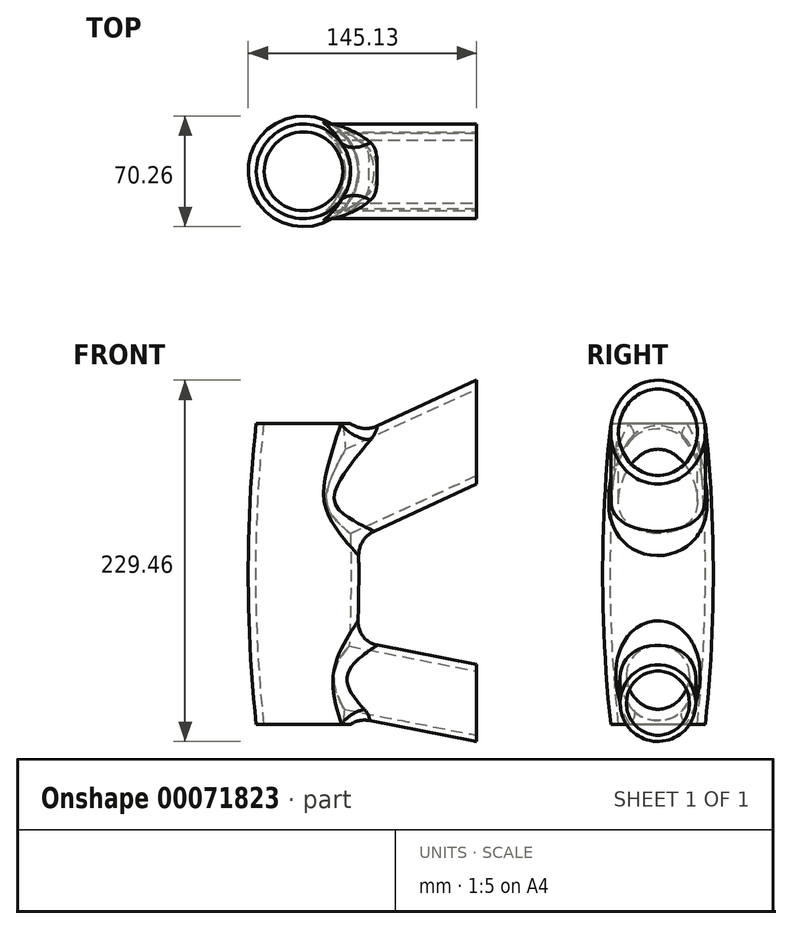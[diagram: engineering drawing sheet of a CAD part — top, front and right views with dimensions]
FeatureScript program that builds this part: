
annotation { "Feature Type Name" : "Feature", "Feature Type Description" : "" }
export const myFeature = defineFeature(function(context is Context, id is Id, definition is map)
    precondition{}
    {
        {
            var Q0;
            Q0=qCreatedBy(makeId("Front.planeOp"),FACE);
            var sketch = newSketch(context, id + "F0", { "sketchPlane" : qUnion([Q0])});
            skLineSegment(sketch, "E0", {"start": v(0, -80) * mm, "end": v(-30, -80) * mm, "construction": true});
            skLineSegment(sketch, "E1", {"start": v(0, 111) * mm, "end": v(-30, 111) * mm, "construction": true});
            skLineSegment(sketch, "E2", {"start": v(0, 111) * mm, "end": v(0, 0) * mm, "construction": true});
            skLineSegment(sketch, "E3", {"start": v(0, 0) * mm, "end": v(0, -80) * mm, "construction": true});
            skLineSegment(sketch, "E4", {"start": v(0, 0) * mm, "end": v(-35, 0) * mm, "construction": true});
            skArc(sketch, "E5", {"start": v(-30, 111) * mm, "mid": v(-35.13, 15.5) * mm, "end": v(-30, -80) * mm});
            skLineSegment(sketch, "E6", {"start": v(0, 0) * mm, "end": v(-25.5, 0) * mm, "construction": true});
            skLineSegment(sketch, "E7", {"start": v(0, 111) * mm, "end": v(-20.5, 111) * mm, "construction": true});
            skLineSegment(sketch, "E8", {"start": v(0, -80) * mm, "end": v(-20.5, -80) * mm, "construction": true});
            skLineSegment(sketch, "E9", {"start": v(-20.5, 111) * mm, "end": v(-30, 111) * mm});
            skLineSegment(sketch, "E10", {"start": v(-20.5, -80) * mm, "end": v(-30, -80) * mm});
            skLineSegment(sketch, "E11", {"start": v(-20.5, 111) * mm, "end": v(0, 111) * mm});
            skLineSegment(sketch, "E12", {"start": v(0, 111) * mm, "end": v(0, -80) * mm});
            skLineSegment(sketch, "E13", {"start": v(0, -80) * mm, "end": v(-20.5, -80) * mm});
            skSolve(sketch);
        }
        {
            var Q0;
            Q0=makeQuery(id+"F0.imprint","IMPRINT",FACE,{"disambiguationData":[TD([[makeQuery(id+"F0.imprint","IMPRINT",EDGE,{"derivedFrom":sQuery(id+"F0.wireOp",EDGE,"E5")}),1.0]])]});
            var Q1;
            Q1=sQuery(id+"F0.wireOp",EDGE,"E2");
            revolve(context, id + "F1", {"entities" : qUnion([Q0]), "axis" : qUnion([Q1]), "revolveType" : RevolveType.FULL});
        }
        {
            var Q0;
            Q0=qCreatedBy(makeId("Front.planeOp"),FACE);
            var sketch = newSketch(context, id + "F2", { "sketchPlane" : qUnion([Q0])});
            skLineSegment(sketch, "E14", {"start": v(0, 0) * mm, "end": v(0, 55) * mm, "construction": true});
            skLineSegment(sketch, "E15", {"start": v(0, 55) * mm, "end": v(154.46, 126) * mm, "construction": true});
            skLineSegment(sketch, "E16", {"start": v(0, 55) * mm, "end": v(0, 126) * mm, "construction": true});
            skLineSegment(sketch, "E17", {"start": v(0, 126) * mm, "end": v(154.46, 126) * mm, "construction": true});
            skLineSegment(sketch, "E18", {"start": v(154.46, 126) * mm, "end": v(167, 98.74) * mm, "construction": true});
            skLineSegment(sketch, "E19", {"start": v(0, 55) * mm, "end": v(12.53, 27.74) * mm, "construction": true});
            skLineSegment(sketch, "E20", {"start": v(154.46, 126) * mm, "end": v(164.07, 105.1) * mm, "construction": true});
            skLineSegment(sketch, "E21", {"start": v(0, 55) * mm, "end": v(9.6, 34.1) * mm, "construction": true});
            skLineSegment(sketch, "E22", {"start": v(12.53, 27.74) * mm, "end": v(167, 98.74) * mm});
            skLineSegment(sketch, "E23", {"start": v(9.6, 34.1) * mm, "end": v(12.53, 27.74) * mm});
            skLineSegment(sketch, "E24", {"start": v(164.07, 105.1) * mm, "end": v(167, 98.74) * mm});
            skLineSegment(sketch, "E25", {"start": v(9.6, 34.1) * mm, "end": v(0, 55) * mm});
            skLineSegment(sketch, "E26", {"start": v(0, 55) * mm, "end": v(154.46, 126) * mm});
            skLineSegment(sketch, "E27", {"start": v(154.46, 126) * mm, "end": v(164.07, 105.1) * mm});
            skSolve(sketch);
        }
        {
            var Q0;
            Q0=makeQuery(id+"F2.imprint","IMPRINT",FACE,{"disambiguationData":[TD([[makeQuery(id+"F2.imprint","IMPRINT",EDGE,{"derivedFrom":sQuery(id+"F2.wireOp",EDGE,"E22")}),1.0]])]});
            var Q1;
            Q1=sQuery(id+"F2.wireOp",EDGE,"E15");
            revolve(context, id + "F3", {"operationType" : NewBodyOperationType.ADD, "entities" : qUnion([Q0]), "axis" : qUnion([Q1]), "revolveType" : RevolveType.FULL});
        }
        {
            var Q0;
            Q0=makeQuery(id+"F3.boolean.opBoolean","SPLIT",FACE,{"disambiguationData":[TD([makeQuery(id+"F1.opRevolve","SWEPT_FACE",FACE,{"disambiguationData":[OSD([sQuery(id+"F0.wireOp",EDGE,"E5")])]})])],"derivedFrom":makeQuery(id+"F3.opRevolve","SWEPT_FACE",FACE,{"disambiguationData":[OSD([sQuery(id+"F2.wireOp",EDGE,"E22")])]})});
            fillet(context, id + "F4", {"entities" : qUnion([Q0]), "radius" : 16.8 * mm, "allowEdgeOverflow" : false});
        }
        {
            var Q0;
            Q0=qCreatedBy(makeId("Front.planeOp"),FACE);
            var sketch = newSketch(context, id + "F5", { "sketchPlane" : qUnion([Q0])});
            skLineSegment(sketch, "E28", {"start": v(0, 0) * mm, "end": v(0, -45) * mm, "construction": true});
            skLineSegment(sketch, "E29", {"start": v(0, -45) * mm, "end": v(0, -70) * mm, "construction": true});
            skLineSegment(sketch, "E30", {"start": v(0, -45) * mm, "end": v(127.57, -70) * mm, "construction": true});
            skLineSegment(sketch, "E31", {"start": v(0, -70) * mm, "end": v(127.57, -70) * mm, "construction": true});
            skLineSegment(sketch, "E32", {"start": v(127.57, -70) * mm, "end": v(122.96, -93.55) * mm, "construction": true});
            skLineSegment(sketch, "E33", {"start": v(0, -45) * mm, "end": v(-4.62, -68.55) * mm, "construction": true});
            skLineSegment(sketch, "E34", {"start": v(127.57, -70) * mm, "end": v(124.4, -86.2) * mm, "construction": true});
            skLineSegment(sketch, "E35", {"start": v(0, -45) * mm, "end": v(-3.17, -61.2) * mm, "construction": true});
            skLineSegment(sketch, "E36", {"start": v(-4.62, -68.55) * mm, "end": v(-3.17, -61.2) * mm});
            skLineSegment(sketch, "E37", {"start": v(124.4, -86.2) * mm, "end": v(122.96, -93.55) * mm});
            skLineSegment(sketch, "E38", {"start": v(122.96, -93.55) * mm, "end": v(-4.62, -68.55) * mm});
            skLineSegment(sketch, "E39", {"start": v(-3.17, -61.2) * mm, "end": v(0, -45) * mm});
            skLineSegment(sketch, "E40", {"start": v(0, -45) * mm, "end": v(127.57, -70) * mm});
            skLineSegment(sketch, "E41", {"start": v(127.57, -70) * mm, "end": v(124.4, -86.2) * mm});
            skSolve(sketch);
        }
        {
            var Q0;
            Q0=makeQuery(id+"F5.imprint","IMPRINT",FACE,{"disambiguationData":[TD([[makeQuery(id+"F5.imprint","IMPRINT",EDGE,{"derivedFrom":sQuery(id+"F5.wireOp",EDGE,"E36")}),-1.0]])]});
            var Q1;
            Q1=sQuery(id+"F5.wireOp",EDGE,"E30");
            revolve(context, id + "F6", {"operationType" : NewBodyOperationType.ADD, "entities" : qUnion([Q0]), "axis" : qUnion([Q1]), "revolveType" : RevolveType.FULL});
        }
        {
            var Q0;
            Q0=makeQuery(id+"F6.boolean.opBoolean","SPLIT",FACE,{"disambiguationData":[TD([makeQuery(id+"F1.opRevolve","SWEPT_FACE",FACE,{"disambiguationData":[OSD([sQuery(id+"F0.wireOp",EDGE,"E5")])]})])],"derivedFrom":makeQuery(id+"F6.opRevolve","SWEPT_FACE",FACE,{"disambiguationData":[OSD([sQuery(id+"F5.wireOp",EDGE,"E38")])]})});
            fillet(context, id + "F7", {"entities" : qUnion([Q0]), "radius" : 15.2 * mm, "tangentPropagation" : true, "allowEdgeOverflow" : false});
        }
        {
            var Q0;
            Q0=qCreatedBy(makeId("Right.planeOp"),FACE);
            cPlane(context, id + "F8", {"entities" : qUnion([Q0]), "cplaneType" : CPlaneType.OFFSET, "offset" : 110 * mm, "width" : 150 * mm, "height" : 150 * mm});
        }
        {
            var Q0;
            Q0=qCreatedBy(id+"F8.planeOp",FACE);
            var sketch = newSketch(context, id + "F9", { "sketchPlane" : qUnion([Q0])});
            skLineSegment(sketch, "E42.bottom", {"start": v(84.13, 151.41) * mm, "end": v(-116.97, 151.41) * mm});
            skLineSegment(sketch, "E42.top", {"start": v(84.13, -97.03) * mm, "end": v(-116.97, -97.03) * mm});
            skLineSegment(sketch, "E42.left", {"start": v(84.13, 151.41) * mm, "end": v(84.13, -97.03) * mm});
            skLineSegment(sketch, "E42.right", {"start": v(-116.97, 151.41) * mm, "end": v(-116.97, -97.03) * mm});
            skSolve(sketch);
        }
        {
            var Q0;
            Q0 = qSketchRegion(id + "F9", true);
            extrude(context, id + "F10", {"entities" : qUnion([Q0]), "operationType" : NewBodyOperationType.REMOVE, "depth" : 100 * mm});
        }
        {
            var Q0;
            Q0=qCreatedBy(makeId("Front.planeOp"),FACE);
            var sketch = newSketch(context, id + "F11", { "sketchPlane" : qUnion([Q0])});
            skLineSegment(sketch, "E43", {"start": v(0, 0) * mm, "end": v(0, -80) * mm, "construction": true});
            skLineSegment(sketch, "E44", {"start": v(0, 0) * mm, "end": v(0, 111) * mm, "construction": true});
            skLineSegment(sketch, "E45", {"start": v(0, 111) * mm, "end": v(-25, 111) * mm});
            skLineSegment(sketch, "E46", {"start": v(0, -80) * mm, "end": v(-25, -80) * mm});
            skLineSegment(sketch, "E47", {"start": v(0, 0) * mm, "end": v(-30, 0) * mm, "construction": true});
            skArc(sketch, "E48", {"start": v(-25, 111) * mm, "mid": v(-30.13, 15.5) * mm, "end": v(-25, -80) * mm});
            skLineSegment(sketch, "E49", {"start": v(-25, -80) * mm, "end": v(0, -80) * mm});
            skLineSegment(sketch, "E50", {"start": v(0, -80) * mm, "end": v(0, 111) * mm});
            skSolve(sketch);
        }
        {
            var Q0;
            Q0 = qSketchRegion(id + "F11", true);
            var Q1;
            Q1=sQuery(id+"F11.wireOp",EDGE,"E50");
            revolve(context, id + "F12", {"operationType" : NewBodyOperationType.REMOVE, "entities" : qUnion([Q0]), "axis" : qUnion([Q1]), "revolveType" : RevolveType.FULL, "oppositeDirection" : true});
        }
        {
            var Q0;
            Q0=qCreatedBy(makeId("Front.planeOp"),FACE);
            var sketch = newSketch(context, id + "F13", { "sketchPlane" : qUnion([Q0])});
            skLineSegment(sketch, "E51", {"start": v(0, 0) * mm, "end": v(0, -45) * mm, "construction": true});
            skLineSegment(sketch, "E52", {"start": v(0, -45) * mm, "end": v(0, -70) * mm, "construction": true});
            skLineSegment(sketch, "E53", {"start": v(0, -45) * mm, "end": v(127.57, -70) * mm, "construction": true});
            skLineSegment(sketch, "E54", {"start": v(0, -70) * mm, "end": v(127.57, -70) * mm, "construction": true});
            skLineSegment(sketch, "E55", {"start": v(127.57, -70) * mm, "end": v(123.73, -89.63) * mm, "construction": true});
            skLineSegment(sketch, "E56", {"start": v(0, -45) * mm, "end": v(-3.85, -64.63) * mm, "construction": true});
            skLineSegment(sketch, "E57", {"start": v(127.57, -70) * mm, "end": v(124.4, -86.2) * mm, "construction": true});
            skLineSegment(sketch, "E58", {"start": v(0, -45) * mm, "end": v(-3.17, -61.2) * mm, "construction": true});
            skLineSegment(sketch, "E59", {"start": v(-3.85, -64.63) * mm, "end": v(-3.17, -61.2) * mm});
            skLineSegment(sketch, "E60", {"start": v(124.4, -86.2) * mm, "end": v(123.73, -89.63) * mm});
            skLineSegment(sketch, "E61", {"start": v(123.73, -89.63) * mm, "end": v(-3.85, -64.63) * mm});
            skLineSegment(sketch, "E62", {"start": v(-3.17, -61.2) * mm, "end": v(0, -45) * mm});
            skLineSegment(sketch, "E63", {"start": v(0, -45) * mm, "end": v(127.57, -70) * mm});
            skLineSegment(sketch, "E64", {"start": v(127.57, -70) * mm, "end": v(124.4, -86.2) * mm});
            skSolve(sketch);
        }
        {
            var Q0;
            Q0=makeQuery(id+"F13.imprint","IMPRINT",FACE,{"disambiguationData":[TD([[makeQuery(id+"F13.imprint","IMPRINT",EDGE,{"derivedFrom":sQuery(id+"F13.wireOp",EDGE,"E59")}),-1.0]])]});
            var Q1;
            Q1=sQuery(id+"F13.wireOp",EDGE,"E63");
            revolve(context, id + "F14", {"operationType" : NewBodyOperationType.REMOVE, "entities" : qUnion([Q0]), "axis" : qUnion([Q1]), "revolveType" : RevolveType.FULL, "oppositeDirection" : true});
        }
        {
            var Q0;
            Q0=qCreatedBy(makeId("Front.planeOp"),FACE);
            var sketch = newSketch(context, id + "F15", { "sketchPlane" : qUnion([Q0])});
            skLineSegment(sketch, "E65", {"start": v(0, 0) * mm, "end": v(0, 55) * mm, "construction": true});
            skLineSegment(sketch, "E66", {"start": v(0, 55) * mm, "end": v(154.46, 126) * mm, "construction": true});
            skLineSegment(sketch, "E67", {"start": v(0, 55) * mm, "end": v(0, 126) * mm, "construction": true});
            skLineSegment(sketch, "E68", {"start": v(0, 126) * mm, "end": v(154.46, 126) * mm, "construction": true});
            skLineSegment(sketch, "E69", {"start": v(154.46, 126) * mm, "end": v(164.9, 103.28) * mm, "construction": true});
            skLineSegment(sketch, "E70", {"start": v(0, 55) * mm, "end": v(10.44, 32.28) * mm, "construction": true});
            skLineSegment(sketch, "E71", {"start": v(154.46, 126) * mm, "end": v(164.07, 105.1) * mm, "construction": true});
            skLineSegment(sketch, "E72", {"start": v(0, 55) * mm, "end": v(9.6, 34.1) * mm, "construction": true});
            skLineSegment(sketch, "E73", {"start": v(10.44, 32.28) * mm, "end": v(164.9, 103.28) * mm});
            skLineSegment(sketch, "E74", {"start": v(9.6, 34.1) * mm, "end": v(10.44, 32.28) * mm});
            skLineSegment(sketch, "E75", {"start": v(164.07, 105.1) * mm, "end": v(164.9, 103.28) * mm});
            skLineSegment(sketch, "E76", {"start": v(9.6, 34.1) * mm, "end": v(0, 55) * mm});
            skLineSegment(sketch, "E77", {"start": v(0, 55) * mm, "end": v(154.46, 126) * mm});
            skLineSegment(sketch, "E78", {"start": v(154.46, 126) * mm, "end": v(164.07, 105.1) * mm});
            skSolve(sketch);
        }
        {
            var Q0;
            Q0=makeQuery(id+"F15.imprint","IMPRINT",FACE,{"disambiguationData":[TD([[makeQuery(id+"F15.imprint","IMPRINT",EDGE,{"derivedFrom":sQuery(id+"F15.wireOp",EDGE,"E73")}),1.0]])]});
            var Q1;
            Q1=sQuery(id+"F15.wireOp",EDGE,"E77");
            revolve(context, id + "F16", {"operationType" : NewBodyOperationType.REMOVE, "entities" : qUnion([Q0]), "axis" : qUnion([Q1]), "revolveType" : RevolveType.FULL, "oppositeDirection" : true});
        }
    });
